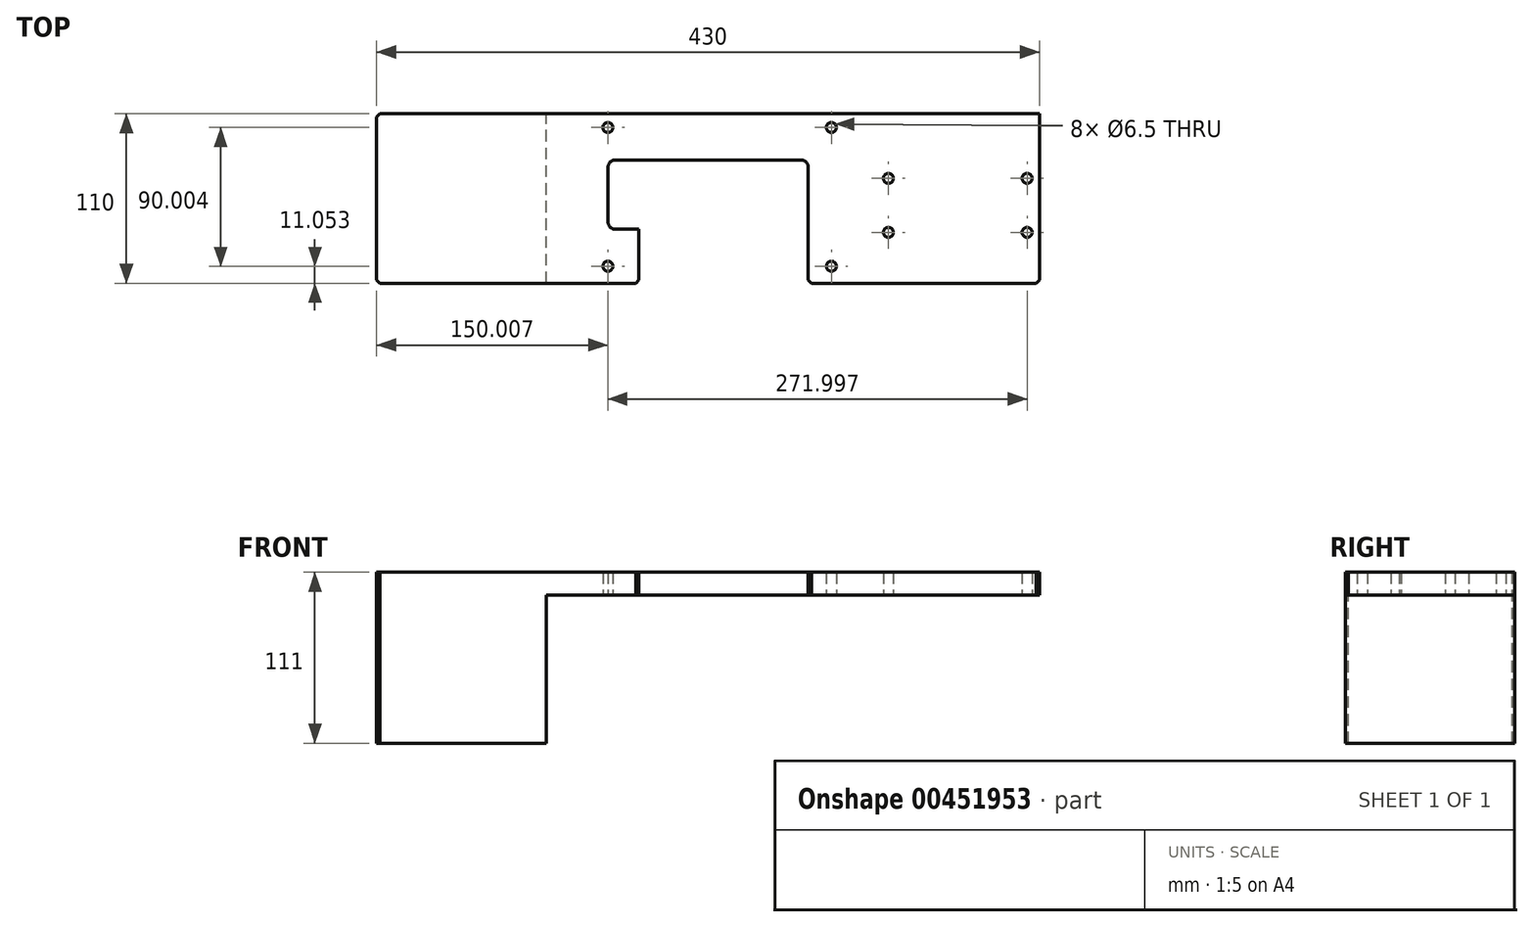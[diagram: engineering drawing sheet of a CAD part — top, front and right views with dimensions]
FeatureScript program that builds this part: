
annotation { "Feature Type Name" : "Feature", "Feature Type Description" : "" }
export const myFeature = defineFeature(function(context is Context, id is Id, definition is map)
    precondition{}
    {
        {
            var Q0;
            Q0=qCreatedBy(makeId("Top.planeOp"),FACE);
            var sketch = newSketch(context, id + "F0", { "sketchPlane" : qUnion([Q0])});
            skLineSegment(sketch, "E0.bottom", {"start": v(-378.56, 83.75) * mm, "end": v(51.44, 83.75) * mm});
            skLineSegment(sketch, "E0.top", {"start": v(-378.56, -26.25) * mm, "end": v(51.44, -26.25) * mm});
            skLineSegment(sketch, "E0.left", {"start": v(-378.56, 83.75) * mm, "end": v(-378.56, -26.25) * mm});
            skLineSegment(sketch, "E0.right", {"start": v(51.44, 83.75) * mm, "end": v(51.44, -26.25) * mm});
            skSolve(sketch);
        }
        {
            var Q0;
            Q0=makeQuery(id+"F0.imprint","IMPRINT",FACE,{"disambiguationData":[TD([[makeQuery(id+"F0.imprint","IMPRINT",EDGE,{"derivedFrom":sQuery(id+"F0.wireOp",EDGE,"E0.bottom")}),-1.0]])]});
            extrude(context, id + "F1", {"entities" : qUnion([Q0]), "depth" : 15 * mm});
        }
        {
            var Q0;
            Q0=qCreatedBy(makeId("Top.planeOp"),FACE);
            var sketch = newSketch(context, id + "F2", { "sketchPlane" : qUnion([Q0])});
            skLineSegment(sketch, "E1.bottom", {"start": v(-228.56, 53.75) * mm, "end": v(-98.56, 53.75) * mm});
            skLineSegment(sketch, "E1.top", {"start": v(-228.56, 8.75) * mm, "end": v(-98.56, 8.75) * mm});
            skLineSegment(sketch, "E1.left", {"start": v(-228.56, 53.75) * mm, "end": v(-228.56, 8.75) * mm});
            skLineSegment(sketch, "E1.right", {"start": v(-98.56, 53.75) * mm, "end": v(-98.56, 8.75) * mm});
            skSolve(sketch);
        }
        {
            var Q0;
            Q0=makeQuery(id+"F2.imprint","IMPRINT",FACE,{"disambiguationData":[TD([[makeQuery(id+"F2.imprint","IMPRINT",EDGE,{"derivedFrom":sQuery(id+"F2.wireOp",EDGE,"E1.bottom")}),-1.0]])]});
            extrude(context, id + "F3", {"entities" : qUnion([Q0]), "operationType" : NewBodyOperationType.REMOVE, "depth" : 25 * mm});
        }
        {
            var Q0;
            Q0=qCreatedBy(makeId("Top.planeOp"),FACE);
            var sketch = newSketch(context, id + "F4", { "sketchPlane" : qUnion([Q0])});
            skLineSegment(sketch, "E2.bottom", {"start": v(-98.56, 12.25) * mm, "end": v(-208.56, 12.25) * mm});
            skLineSegment(sketch, "E2.top", {"start": v(-98.56, -33.65) * mm, "end": v(-208.56, -33.65) * mm});
            skLineSegment(sketch, "E2.left", {"start": v(-98.56, 12.25) * mm, "end": v(-98.56, -33.65) * mm});
            skLineSegment(sketch, "E2.right", {"start": v(-208.56, 12.25) * mm, "end": v(-208.56, -33.65) * mm});
            skSolve(sketch);
        }
        {
            var Q0;
            Q0 = qSketchRegion(id + "F4", true);
            extrude(context, id + "F5", {"entities" : qUnion([Q0]), "operationType" : NewBodyOperationType.REMOVE, "depth" : 25 * mm});
        }
        {
            var Q0;
            Q0=makeQuery(id+"F3.boolean.opBoolean","COPY",EDGE,{"derivedFrom":makeQuery(id+"F3.opExtrude","SWEPT_EDGE",EDGE,{"disambiguationData":[OSD([sQuery(id+"F2.wireOp",EDGE,"E1.bottom"),sQuery(id+"F2.wireOp",EDGE,"E1.left")])]})});
            var Q1;
            Q1=makeQuery(id+"F3.boolean.opBoolean","COPY",EDGE,{"derivedFrom":makeQuery(id+"F3.opExtrude","SWEPT_EDGE",EDGE,{"disambiguationData":[OSD([sQuery(id+"F2.wireOp",EDGE,"E1.bottom"),sQuery(id+"F2.wireOp",EDGE,"E1.right")])]})});
            var Q2;
            Q2=makeQuery(id+"F3.boolean.opBoolean","COPY",EDGE,{"derivedFrom":makeQuery(id+"F3.opExtrude","SWEPT_EDGE",EDGE,{"disambiguationData":[OSD([sQuery(id+"F2.wireOp",EDGE,"E1.top"),sQuery(id+"F2.wireOp",EDGE,"E1.left")])]})});
            fillet(context, id + "F6", {"entities" : qUnion([Q0, Q1, Q2]), "radius" : 5 * mm, "tangentPropagation" : true, "allowEdgeOverflow" : false});
        }
        {
            var Q0;
            Q0=makeQuery(id+"F5.boolean.opBoolean","INTERSECT",EDGE,{"derivedFrom":[makeQuery(id+"F1.opExtrude","SWEPT_FACE",FACE,{"disambiguationData":[OSD([sQuery(id+"F0.wireOp",EDGE,"E0.top")])]}),makeQuery(id+"F5.opExtrude","SWEPT_FACE",FACE,{"disambiguationData":[OSD([sQuery(id+"F4.wireOp",EDGE,"E2.right")])]})]});
            var Q1;
            Q1=makeQuery(id+"F5.boolean.opBoolean","INTERSECT",EDGE,{"derivedFrom":[makeQuery(id+"F1.opExtrude","SWEPT_FACE",FACE,{"disambiguationData":[OSD([sQuery(id+"F0.wireOp",EDGE,"E0.top")])]}),makeQuery(id+"F5.opExtrude","SWEPT_FACE",FACE,{"disambiguationData":[OSD([sQuery(id+"F4.wireOp",EDGE,"E2.left")])]})]});
            var Q2;
            Q2=makeQuery(id+"F1.opExtrude","SWEPT_EDGE",EDGE,{"disambiguationData":[OSD([sQuery(id+"F0.wireOp",EDGE,"E0.top"),sQuery(id+"F0.wireOp",EDGE,"E0.left")])]});
            var Q3;
            Q3=makeQuery(id+"F1.opExtrude","SWEPT_EDGE",EDGE,{"disambiguationData":[OSD([sQuery(id+"F0.wireOp",EDGE,"E0.bottom"),sQuery(id+"F0.wireOp",EDGE,"E0.left")])]});
            var Q4;
            Q4=makeQuery(id+"F1.opExtrude","SWEPT_EDGE",EDGE,{"disambiguationData":[OSD([sQuery(id+"F0.wireOp",EDGE,"E0.top"),sQuery(id+"F0.wireOp",EDGE,"E0.right")])]});
            chamfer(context, id + "F7", {"entities" : qUnion([Q0, Q1, Q2, Q3, Q4]), "width" : 2 * mm, "tangentPropagation" : true});
        }
        {
            var Q0;
            Q0=makeQuery(id+"F1.opExtrude","CAP_FACE",FACE,{"disambiguationData":[OSD([sQuery(id+"F0.wireOp",EDGE,"E0.bottom"),sQuery(id+"F0.wireOp",EDGE,"E0.top"),sQuery(id+"F0.wireOp",EDGE,"E0.left"),sQuery(id+"F0.wireOp",EDGE,"E0.right")])],"isStart":true});
            var sketch = newSketch(context, id + "F8", { "sketchPlane" : qUnion([Q0])});
            skLineSegment(sketch, "E3.bottom", {"start": v(-378.56, 26.25) * mm, "end": v(-268.56, 26.25) * mm});
            skLineSegment(sketch, "E3.top", {"start": v(-378.56, -83.75) * mm, "end": v(-268.56, -83.75) * mm});
            skLineSegment(sketch, "E3.left", {"start": v(-378.56, 26.25) * mm, "end": v(-378.56, -83.75) * mm});
            skLineSegment(sketch, "E3.right", {"start": v(-268.56, 26.25) * mm, "end": v(-268.56, -83.75) * mm});
            skSolve(sketch);
        }
        {
            var Q0;
            {var subQ0=sQuery(id+"F8.wireOp",EDGE,"E3.right");Q0=makeQuery(id+"F8.imprint","IMPRINT",FACE,{"disambiguationData":[TD([[makeQuery(id+"F8.imprint","IMPRINT",EDGE,{"derivedFrom":subQ0}),-1.0]])]});}
            extrude(context, id + "F9", {"entities" : qUnion([Q0]), "operationType" : NewBodyOperationType.ADD, "depth" : 96 * mm});
        }
        {
            var Q0;
            Q0=qCreatedBy(makeId("Top.planeOp"),FACE);
            var sketch = newSketch(context, id + "F10", { "sketchPlane" : qUnion([Q0])});
            skLineSegment(sketch, "E4", {"start": v(-228.56, 145.3) * mm, "end": v(-228.56, -54.7) * mm, "construction": true});
            skLineSegment(sketch, "E5", {"start": v(-83.56, 145.3) * mm, "end": v(-83.56, -54.7) * mm, "construction": true});
            skLineSegment(sketch, "E6", {"start": v(-259.25, 126.8) * mm, "end": v(-15.2, 126.8) * mm, "construction": true});
            skLineSegment(sketch, "E7", {"start": v(-259.25, 126.8) * mm, "end": v(-259.25, 74.8) * mm, "construction": true});
            skLineSegment(sketch, "E8", {"start": v(-259.25, 74.8) * mm, "end": v(-38.18, 74.8) * mm, "construction": true});
            skLineSegment(sketch, "E9", {"start": v(-38.18, -15.2) * mm, "end": v(-259.25, -15.2) * mm, "construction": true});
            skSolve(sketch);
        }
        {
            var Q0;
            Q0=qCreatedBy(makeId("Top.planeOp"),FACE);
            var sketch = newSketch(context, id + "F11", { "sketchPlane" : qUnion([Q0])});
            skCircle(sketch, "E10", {"center": v(-228.55, 74.8) * mm, "radius": 3.25 * mm});
            skCircle(sketch, "E11", {"center": v(-228.5, -15.16) * mm, "radius": 3.25 * mm});
            skCircle(sketch, "E12", {"center": v(-83.54, -15.2) * mm, "radius": 3.25 * mm});
            skCircle(sketch, "E13", {"center": v(-83.55, 74.8) * mm, "radius": 3.25 * mm});
            skSolve(sketch);
        }
        {
            var Q0;
            Q0=makeQuery(id+"F11.imprint","IMPRINT",FACE,{"disambiguationData":[TD([[makeQuery(id+"F11.imprint","IMPRINT",EDGE,{"derivedFrom":sQuery(id+"F11.wireOp",EDGE,"E11")}),1.0]])]});
            var Q1;
            Q1=makeQuery(id+"F11.imprint","IMPRINT",FACE,{"disambiguationData":[TD([[makeQuery(id+"F11.imprint","IMPRINT",EDGE,{"derivedFrom":sQuery(id+"F11.wireOp",EDGE,"E10")}),1.0]])]});
            var Q2;
            Q2=makeQuery(id+"F11.imprint","IMPRINT",FACE,{"disambiguationData":[TD([[makeQuery(id+"F11.imprint","IMPRINT",EDGE,{"derivedFrom":sQuery(id+"F11.wireOp",EDGE,"E13")}),1.0]])]});
            var Q3;
            Q3=makeQuery(id+"F11.imprint","IMPRINT",FACE,{"disambiguationData":[TD([[makeQuery(id+"F11.imprint","IMPRINT",EDGE,{"derivedFrom":sQuery(id+"F11.wireOp",EDGE,"E12")}),1.0]])]});
            extrude(context, id + "F12", {"entities" : qUnion([Q0, Q1, Q2, Q3]), "operationType" : NewBodyOperationType.REMOVE, "depth" : 25 * mm});
        }
        {
            var Q0;
            Q0=qCreatedBy(makeId("Top.planeOp"),FACE);
            var sketch = newSketch(context, id + "F13", { "sketchPlane" : qUnion([Q0])});
            skLineSegment(sketch, "E14", {"start": v(-98.56, 20.89) * mm, "end": v(-46.56, 20.89) * mm, "construction": true});
            skLineSegment(sketch, "E15", {"start": v(-46.56, 20.89) * mm, "end": v(-46.56, 97.68) * mm, "construction": true});
            skLineSegment(sketch, "E16", {"start": v(-46.56, 97.68) * mm, "end": v(-46.56, -57.92) * mm, "construction": true});
            skLineSegment(sketch, "E17", {"start": v(-46.56, -57.92) * mm, "end": v(43.44, -57.92) * mm, "construction": true});
            skLineSegment(sketch, "E18", {"start": v(43.44, -57.92) * mm, "end": v(43.44, 97.68) * mm, "construction": true});
            skLineSegment(sketch, "E19", {"start": v(-10.67, 126.8) * mm, "end": v(-10.67, 41.8) * mm, "construction": true});
            skLineSegment(sketch, "E20", {"start": v(-10.67, 41.8) * mm, "end": v(84.7, 41.8) * mm, "construction": true});
            skLineSegment(sketch, "E21", {"start": v(84.7, 41.8) * mm, "end": v(-59.17, 41.8) * mm, "construction": true});
            skLineSegment(sketch, "E22", {"start": v(-59.17, 41.8) * mm, "end": v(-59.17, 6.8) * mm, "construction": true});
            skLineSegment(sketch, "E23", {"start": v(-59.17, 6.8) * mm, "end": v(94.48, 6.8) * mm, "construction": true});
            skCircle(sketch, "E24", {"center": v(-46.56, 41.8) * mm, "radius": 3.25 * mm});
            skCircle(sketch, "E25", {"center": v(43.44, 41.8) * mm, "radius": 3.25 * mm});
            skCircle(sketch, "E26", {"center": v(43.44, 6.8) * mm, "radius": 3.25 * mm});
            skCircle(sketch, "E27", {"center": v(-46.56, 6.8) * mm, "radius": 3.25 * mm});
            skSolve(sketch);
        }
        {
            var Q0;
            Q0=makeQuery(id+"F13.imprint","IMPRINT",FACE,{"disambiguationData":[TD([[makeQuery(id+"F13.imprint","IMPRINT",EDGE,{"derivedFrom":sQuery(id+"F13.wireOp",EDGE,"E27")}),1.0]])]});
            var Q1;
            Q1=makeQuery(id+"F13.imprint","IMPRINT",FACE,{"disambiguationData":[TD([[makeQuery(id+"F13.imprint","IMPRINT",EDGE,{"derivedFrom":sQuery(id+"F13.wireOp",EDGE,"E24")}),1.0]])]});
            var Q2;
            Q2=makeQuery(id+"F13.imprint","IMPRINT",FACE,{"disambiguationData":[TD([[makeQuery(id+"F13.imprint","IMPRINT",EDGE,{"derivedFrom":sQuery(id+"F13.wireOp",EDGE,"E26")}),1.0]])]});
            var Q3;
            Q3=makeQuery(id+"F13.imprint","IMPRINT",FACE,{"disambiguationData":[TD([[makeQuery(id+"F13.imprint","IMPRINT",EDGE,{"derivedFrom":sQuery(id+"F13.wireOp",EDGE,"E25")}),1.0]])]});
            extrude(context, id + "F14", {"entities" : qUnion([Q0, Q1, Q2, Q3]), "operationType" : NewBodyOperationType.REMOVE, "depth" : 25 * mm});
        }
    });
